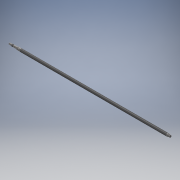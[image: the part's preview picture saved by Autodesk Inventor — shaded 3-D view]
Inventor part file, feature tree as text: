
AUTODESK INVENTOR PART (.ipt)
format: ipt  version: 2018 (Build 220112000, 112)  size: 157,184 bytes
history: native  units: mm
features: other x21, sketch x5, revolve x3, thread x2, extrude x2
ambient origin geometry x8: Origin, YZ Plane, XZ Plane, XY Plane, X Axis, Y Axis, Z Axis, Center Point
bodies: Solid1 (feature_tree)
feature tree (33):
  revolve  "Revolution1"  [1 undecoded]
  thread  "Thread1"  [1 undecoded]
  revolve  "Revolution2"  [1 undecoded]
  thread  "Thread2"  [1 undecoded]
  extrude  "Extrusion1"  TaperAngle=0.0deg  [1 undecoded]
  extrude  "Extrusion2"  [1 undecoded]
  revolve  "Revolution3"  [1 undecoded]
  other  "FSS_XY"
  other  "FSS_YZ"
  other  "FSS_ZX"
  other  "FSS_X"
  other  "FSS_Y"
  other  "FSS_Z"
  other  "FSS_Center"
  other  "SSS_XY"
  other  "SSS_YZ"
  other  "SSS_ZX"
  other  "SSS_X"
  other  "SSS_Y"
  other  "SSS_Z"
  other  "SSS_Center"
  other  "bnt_s_1_XY"
  other  "bnt_s_1_YZ"
  other  "bnt_s_1_ZX"
  other  "bnt_s_1_X"
  other  "bnt_s_1_Y"
  other  "bnt_s_1_Z"
  other  "bnt_s_1_Center"
  sketch  "Sketch_1"  dims[d0=360.0deg d1=1058.0mm d2=0.0mm d3=360.0deg]
  sketch  "Sketch_10"  dims[d4=11.3865mm d5=0.0mm d6=4.0mm d7=0.0mm d8=4.0mm d9=0.0mm]
  sketch  "Sketch_11"  dims[d10=360.0deg d11=0.0mm d12=0.0mm d13=0.0mm]
  sketch  "Sketch_12"
  sketch  "Sketch_16"
note: 7 required parameter values undecoded (feature->parameter linkage not recoverable at this tier; creation-order binding heuristic only, values carry confidence <= 0.55)